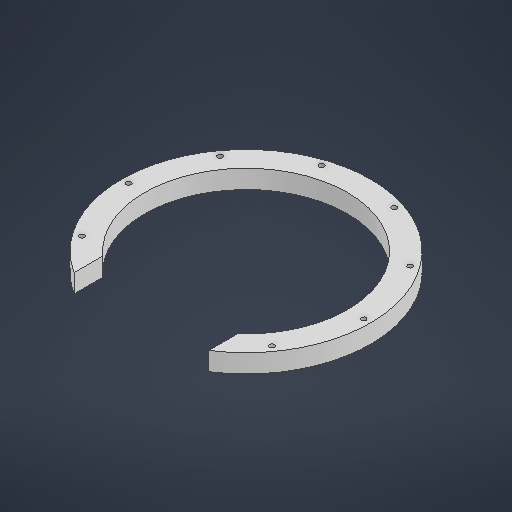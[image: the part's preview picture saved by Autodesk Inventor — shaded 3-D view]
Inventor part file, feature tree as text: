
AUTODESK INVENTOR PART (.ipt)
format: ipt  version: 2025 (Build 290162000, 162)  size: 227,840 bytes
history: native  units: in
note: dims shown in document units (in); Inventor stores cm internally (conversion verified against a paired STEP export)
features: sketch x4, extrude x2, hole x1
ambient origin geometry x8: Origin, YZ Plane, XZ Plane, XY Plane, X Axis, Y Axis, Z Axis, Center Point
bodies: Solid1 (feature_tree)
feature tree (7):
  extrude  "Extrusion1"  Depth=8.6614in
  hole  "Hole1"  [1 undecoded]
  extrude  "Extrusion6"  Depth=3.937in TaperAngle=360.0deg
  sketch  "Sketch1"  dims[d0=10.6299in d1=8.6614in]
  sketch  "Sketch3"  dims[d9=0.1575in d10=3.937in d12=360.0deg]
  sketch  "Sketch Circular Pattern1"  dims[d2=0.7874in d3=0.0in d8=10.0394in]
  sketch  "Sketch7"  dims[d14=0.2165in d15=0.3937in d16=0.1575in d17=0.0787in d18=90.0deg d19=0.315in d20=0.8108in d32=5.753in d33=13.7795in d34=0.0in d35=0.0in d24=0.0197in d25=0.0344in d26=0.0197in d27=0.0344in d30=0.0197in d31=0.0344in]
note: 1 required parameter value undecoded (feature->parameter linkage not recoverable at this tier; creation-order binding heuristic only, values carry confidence <= 0.55)
